# Revit family: Lighting-Proiezione-GEWISS-ESALITE-FL-PROIETTORI-LED_24K_DALI
name_source: partatom
category: Apparecchi per illuminazione
units: mm (PartAtom-declared; Revit-internal decimal feet)

## family parameters
Condiviso = No
Host = Superficie
Punto di calcolo locali = Sì
Quota connettore circolare = Usa diametro
Sorgente d'illuminazione = Sì
Taglio con vuoti quando caricato = No
Tipo di parte = Normale

## types (1)
- Lighting-Proiezione-GEWISS-ESALITE-FL-PROIETTORI-LED_24K_DALI
    Angolo inclinazione = -90.00°
    Applicazione = Interno / Esterno
    Catalogo = LIGHTING
    Catalogo Serie = ESALITE FL - 24K
    Classe di efficienza LED integrati = A ÷ A++
    Classe isolamento = I
    Codice Electrocod = 2444
    Colore = Grigio RAL 9006
    Corrente di pilotaggio. = 0,9A
    Descrizione = ESALITE 24K ELL.5700K PRO+V.GR.DALI
    Emetti da lunghezza linea = 20 mm  [stored 0.0656168 ft]
    File diagramma fotometrico = GWS6455GD57K.IES
    Filtro dei colori = 16777215
    Flusso nominale (lm) = 29000
    Garanzia = 5 anni
    Grado di protezione = IP66
    IDF = 5aec9055-4099-401f-a7fb-c27d525fc254
    IDT = f7a9a771bf584c71b29cfc4a92707170
    Immagine tipo = ESALITE_FL.jpg
    Lampada: = LED - Non sostituibile
    Life time L90B10 (Tq 25°C) = 100000H
    Life time L90B10 (Tq 50°C) = 44000H
    Lumen output (lm) = 22200
    Modello = GWS6455GD57K
    Numero poli = 1
    Ottica = Ellittica
    Peso (kg): = 13,7
    Potenza di sistema = 210W
    Potenza di sitema = Wxxx
    Produttore = GEWISS S.p.A.
    Prospetto di default = 1219 mm
    Resistenza agli urti = IK08
    Resistenza alle sovratensioni : = 8KV in modalità comune; 6KV in modalità differenziale
    SEO = Proiettore
    STAFFA = <Per categoria>
    Scheda Tecnica = https://www.gewiss.com
    Schermo = Vetro temprato
    Temperatura di colore: = 5700 K (CRI>80)
    Temperatura di utilizzo = -30 +50 °C
    Tensione = 220/240 V - 50/60 Hz
    Tipo alimentatore = Driver Led Dali
    URL = https://www.gewiss.com
    V = 0 V
    Variazione temperatura colore lampada con luminosità attenuata = <Nessuno>
    Versione file RFA = 20.11
    Versioni = Luce fredda 5700K

note: [stored X ft] marks values corroborated as IEEE doubles in the binary element streams (Revit-internal decimal feet)

## geometry (parser evidence)
native form markers: Sweep x2
no freeform markers — native parametric forms only
